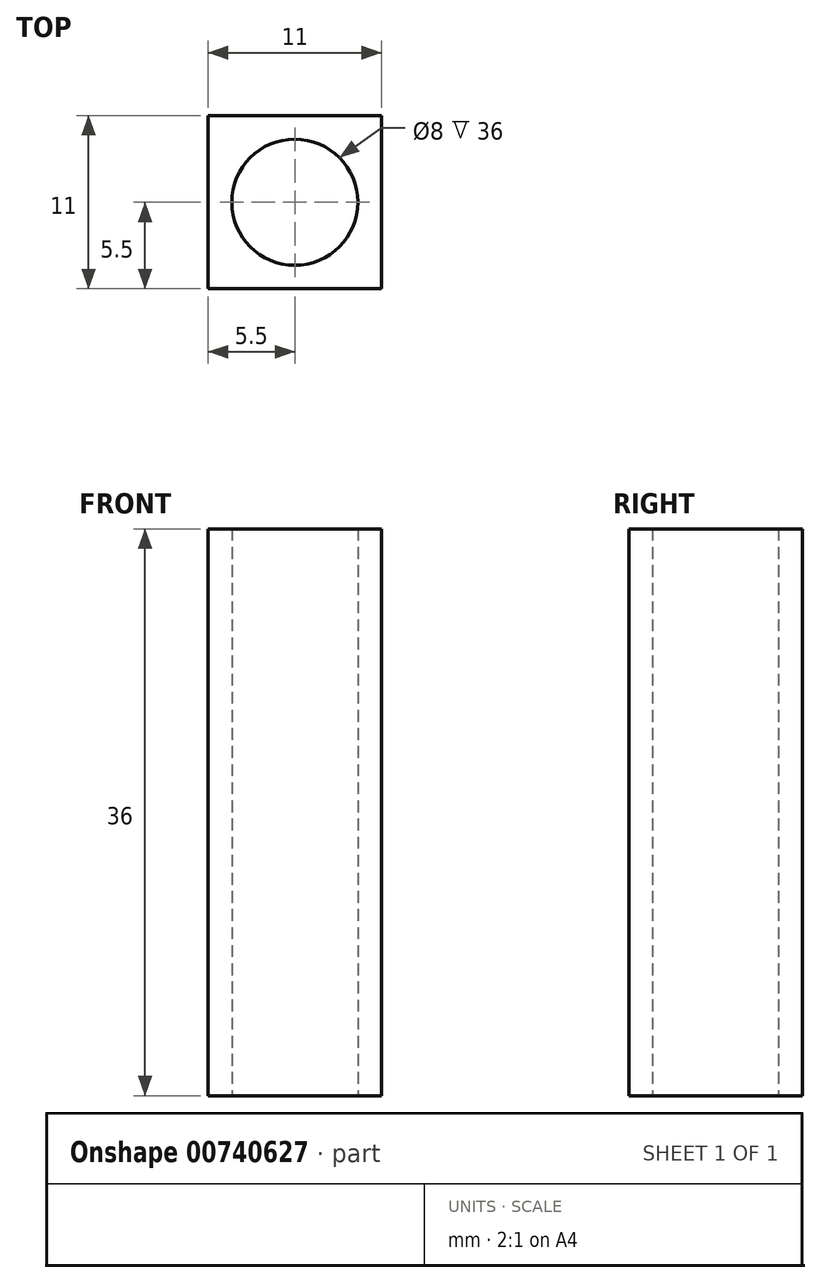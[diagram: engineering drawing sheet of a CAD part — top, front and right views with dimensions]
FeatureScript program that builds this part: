
annotation { "Feature Type Name" : "Feature", "Feature Type Description" : "" }
export const myFeature = defineFeature(function(context is Context, id is Id, definition is map)
    precondition{}
    {
        {
            var Q0;
            Q0=qCreatedBy(makeId("Top.planeOp"),FACE);
            var sketch = newSketch(context, id + "F0", { "sketchPlane" : qUnion([Q0])});
            skLineSegment(sketch, "E0.bottom", {"start": v(5.5, -5.5) * mm, "end": v(-5.5, -5.5) * mm});
            skLineSegment(sketch, "E0.top", {"start": v(5.5, 5.5) * mm, "end": v(-5.5, 5.5) * mm});
            skLineSegment(sketch, "E0.left", {"start": v(5.5, -5.5) * mm, "end": v(5.5, 5.5) * mm});
            skLineSegment(sketch, "E0.right", {"start": v(-5.5, -5.5) * mm, "end": v(-5.5, 5.5) * mm});
            skPoint(sketch, "E0.middle", {"position": v(0, 0) * mm});
            skCircle(sketch, "E1", {"center": v(0, 0) * mm, "radius": 4 * mm});
            skSolve(sketch);
        }
        {
            var Q0;
            Q0=makeQuery(id+"F0.imprint","IMPRINT",FACE,{"disambiguationData":[TD([[makeQuery(id+"F0.imprint","IMPRINT",EDGE,{"derivedFrom":sQuery(id+"F0.wireOp",EDGE,"E0.bottom")}),-1.0]])]});
            extrude(context, id + "F1", {"entities" : qUnion([Q0]), "depth" : 36 * mm, "offsetDistance" : 25 * mm});
        }
    });
